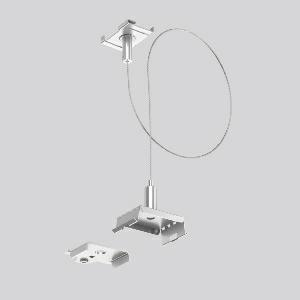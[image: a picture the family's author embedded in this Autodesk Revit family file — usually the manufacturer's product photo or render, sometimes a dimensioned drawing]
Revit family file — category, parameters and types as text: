
# Revit family: linedo_pendelset_1_5m_seil_caddyclip_982665_000_4412
name_source: partatom
category: Lighting Fixtures
units: mm (PartAtom-declared; Revit-internal decimal feet)

## family parameters
Cut with Voids When Loaded = No
Host = Face
Light Source = No
Part Type = Normal
Room Calculation Point = No
Round Connector Dimension = Use Diameter
Shared = No

## types (1)
- LINEDO Pendelset 1,5m Seil Caddyclip
    Apparent Load = 0 VA
    Default Elevation = 1800 mm
    Description = Suspension kit for grid ceilings with steel cable 1,500 mm and caddy clip. Spring steel, blank, for installing continuous line luminaire modules.
Colour: stainless steel
Weight: 75 g
Type of Installation: pendant
    Height = 70 mm
    Lamp = 0 x
    Length = 52 mm  [stored 0.170604 ft]
    Luminous efficacy = 0 lm/W
    Manufacturer = RZB
    ModVariant = No
    Model = 982665.000
    Mounting Place = Ceiling
    Mounting Type = Surface mounted
    Number of Poles = 1
    OnlyDefault = Yes
    Power Factor = 1
    Product Name = LINEDO Pendelset 1,5m Seil Caddyclip
    Product group = Surface mounted continuous line luminaire system
    ProductGroupID = 310
    Protection Class = Protection class
    Protection Degree = Degree of protection
    RLX_Detail_Level = 1
    RLX_Emergency_Light_Flux = 0 lm
    RLX_Emergency_Type = 0
    RLX_Emergency_Type_DB = No
    RlxData = <blob elided: 20177 chars, md5=3b300bdb>
    Standby Power = 0 W
    System Light Flux = 0 lm
    System Power = 0 W
    Type Comments = Product without accessories
    Type Image = 982665.000.jpg
    URL = http://relux.com
    VarID = ---
    Voltage = 0 V
    Weight = 0.00 kg
    Width = 54 mm

note: [stored X ft] marks values corroborated as IEEE doubles in the binary element streams (Revit-internal decimal feet)

## geometry (parser evidence)
native form markers: Blend x4, Sweep x11
no freeform markers — native parametric forms only
